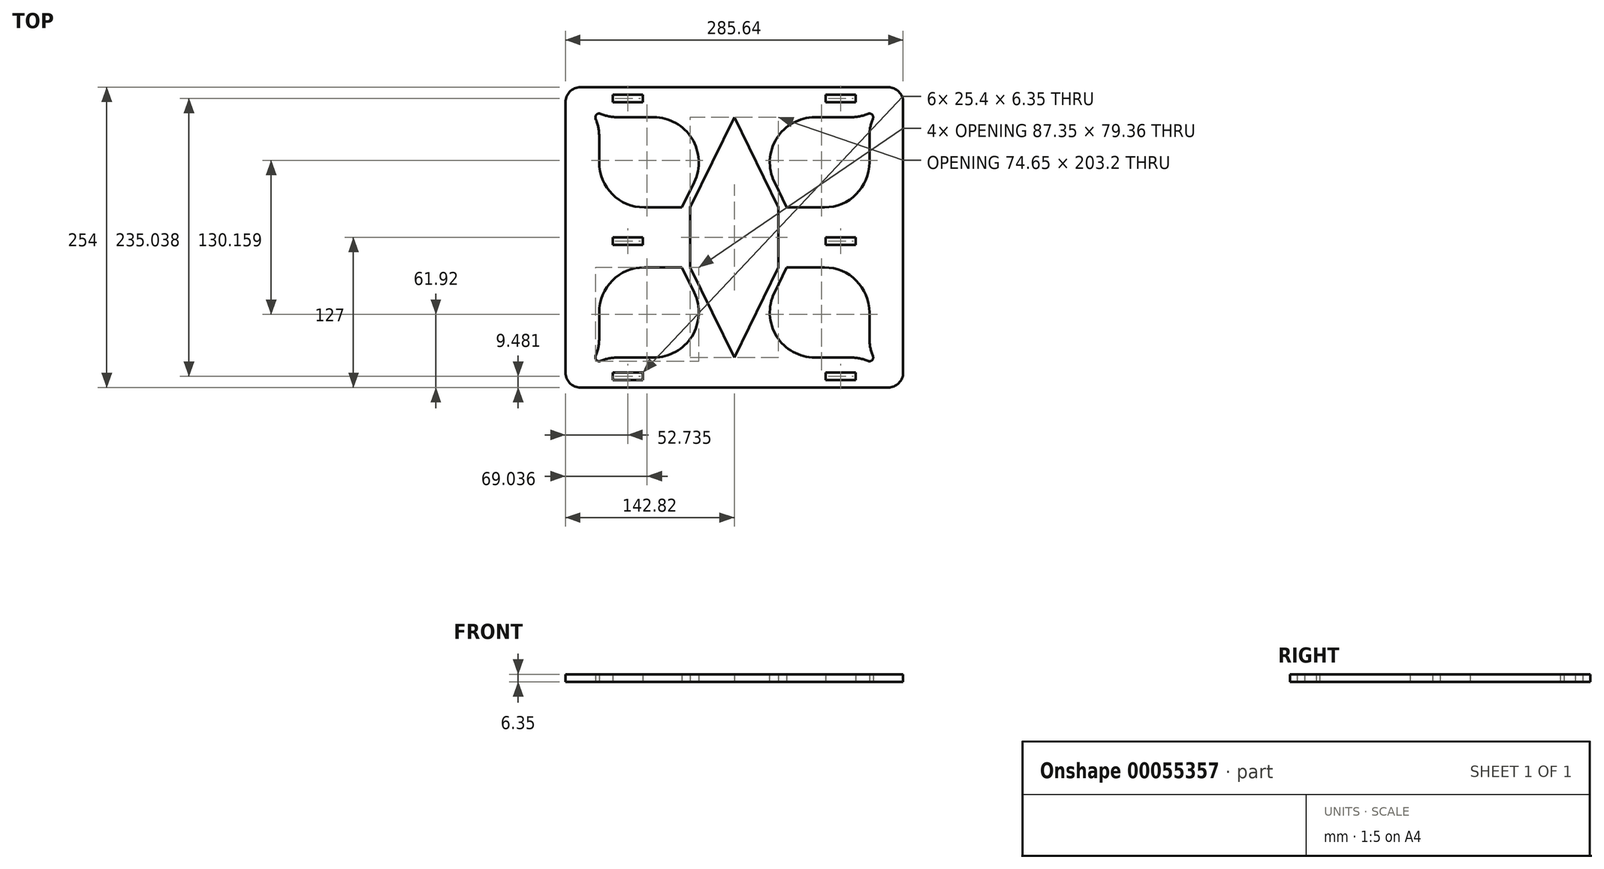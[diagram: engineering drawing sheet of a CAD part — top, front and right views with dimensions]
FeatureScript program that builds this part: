
annotation { "Feature Type Name" : "Feature", "Feature Type Description" : "" }
export const myFeature = defineFeature(function(context is Context, id is Id, definition is map)
    precondition{}
    {
        {
            var Q0;
            Q0=qCreatedBy(makeId("Top.planeOp"),FACE);
            var sketch = newSketch(context, id + "F0", { "sketchPlane" : qUnion([Q0])});
            skLineSegment(sketch, "E0.rect.bottom", {"start": v(130.12, 127) * mm, "end": v(-130.12, 127) * mm});
            skLineSegment(sketch, "E0.rect.top", {"start": v(130.12, -127) * mm, "end": v(-130.12, -127) * mm});
            skLineSegment(sketch, "E0.rect.left", {"start": v(142.82, 114.3) * mm, "end": v(142.82, -114.3) * mm});
            skLineSegment(sketch, "E0.rect.right", {"start": v(-142.82, 114.3) * mm, "end": v(-142.82, -114.3) * mm});
            skPoint(sketch, "E0.rect.middle", {"position": v(0, 0) * mm});
            skLineSegment(sketch, "E1", {"start": v(-142.82, 0) * mm, "end": v(-102.77, 0) * mm, "construction": true});
            skPoint(sketch, "E1.endSnap0", {"position": v(-142.82, 0) * mm});
            skPoint(sketch, "E2.visualSharp", {"position": v(-142.82, 127) * mm});
            skArc(sketch, "E2.filletArc", {"start": v(-130.12, 127) * mm, "mid": v(-139.1, 123.28) * mm, "end": v(-142.82, 114.3) * mm});
            skPoint(sketch, "E3.visualSharp", {"position": v(142.82, 127) * mm});
            skArc(sketch, "E3.filletArc", {"start": v(142.82, 114.3) * mm, "mid": v(139.1, 123.28) * mm, "end": v(130.12, 127) * mm});
            skPoint(sketch, "E4.visualSharp", {"position": v(142.82, -127) * mm});
            skArc(sketch, "E4.filletArc", {"start": v(130.12, -127) * mm, "mid": v(139.1, -123.28) * mm, "end": v(142.82, -114.3) * mm});
            skPoint(sketch, "E5.visualSharp", {"position": v(-142.82, -127) * mm});
            skArc(sketch, "E5.filletArc", {"start": v(-142.82, -114.3) * mm, "mid": v(-139.1, -123.28) * mm, "end": v(-130.12, -127) * mm});
            skLineSegment(sketch, "E6.rect.bottom", {"start": v(114.3, 101.6) * mm, "end": v(-114.3, 101.6) * mm});
            skLineSegment(sketch, "E6.rect.top", {"start": v(114.3, 25.4) * mm, "end": v(-114.3, 25.4) * mm});
            skLineSegment(sketch, "E6.rect.left", {"start": v(114.3, 101.6) * mm, "end": v(114.3, 25.4) * mm});
            skLineSegment(sketch, "E6.rect.right", {"start": v(-114.3, 101.6) * mm, "end": v(-114.3, 25.4) * mm});
            skPoint(sketch, "E6.rect.middle", {"position": v(0, 63.5) * mm});
            skLineSegment(sketch, "E7.MirrorCS", {"start": v(114.3, -101.6) * mm, "end": v(-114.3, -101.6) * mm});
            skLineSegment(sketch, "E8.MirrorCS", {"start": v(114.3, -101.6) * mm, "end": v(114.3, -25.4) * mm});
            skPoint(sketch, "E9.MirrorP", {"position": v(0, -63.5) * mm});
            skLineSegment(sketch, "E10.MirrorCS", {"start": v(-114.3, -101.6) * mm, "end": v(-114.3, -25.4) * mm});
            skLineSegment(sketch, "E11.MirrorCS", {"start": v(114.3, -25.4) * mm, "end": v(-114.3, -25.4) * mm});
            skLineSegment(sketch, "E12.MirrorCS", {"start": v(142.82, 0) * mm, "end": v(102.77, 0) * mm, "construction": true});
            skLineSegment(sketch, "E13.rect.bottom", {"start": v(37.33, 25.4) * mm, "end": v(-37.33, 25.4) * mm});
            skLineSegment(sketch, "E13.rect.top", {"start": v(37.33, -25.4) * mm, "end": v(-37.33, -25.4) * mm});
            skLineSegment(sketch, "E13.rect.left", {"start": v(37.33, 25.4) * mm, "end": v(37.33, -25.4) * mm});
            skLineSegment(sketch, "E13.rect.right", {"start": v(-37.33, 25.4) * mm, "end": v(-37.33, -25.4) * mm});
            skLineSegment(sketch, "E14", {"start": v(0, 101.6) * mm, "end": v(37.33, 25.4) * mm});
            skLineSegment(sketch, "E15.0", {"start": v(7.07, 101.6) * mm, "end": v(44.4, 25.4) * mm});
            skLineSegment(sketch, "E16.MirrorCS", {"start": v(0, 101.6) * mm, "end": v(-37.33, 25.4) * mm});
            skLineSegment(sketch, "E17.MirrorCS", {"start": v(-7.07, 101.6) * mm, "end": v(-44.4, 25.4) * mm});
            skLineSegment(sketch, "E18.MirrorCS", {"start": v(0, -101.6) * mm, "end": v(-37.33, -25.4) * mm});
            skLineSegment(sketch, "E19.MirrorCS", {"start": v(-7.07, -101.6) * mm, "end": v(-44.4, -25.4) * mm});
            skLineSegment(sketch, "E20.MirrorCS", {"start": v(7.07, -101.6) * mm, "end": v(44.4, -25.4) * mm});
            skLineSegment(sketch, "E21.MirrorCS", {"start": v(0, -101.6) * mm, "end": v(37.33, -25.4) * mm});
            skLineSegment(sketch, "E22", {"start": v(-142.82, 101.6) * mm, "end": v(-142.82, 127) * mm, "construction": true});
            skLineSegment(sketch, "E23", {"start": v(-142.82, 63.5) * mm, "end": v(142.82, 63.5) * mm, "construction": true});
            skPoint(sketch, "E23.endSnap0", {"position": v(114.3, 63.5) * mm});
            skCircle(sketch, "E24", {"center": v(-114.3, 101.6) * mm, "radius": 3.18 * mm});
            skCircle(sketch, "E25.MirrorC", {"center": v(114.3, 101.6) * mm, "radius": 3.18 * mm});
            skCircle(sketch, "E26.MirrorC", {"center": v(-114.3, -101.6) * mm, "radius": 3.18 * mm});
            skCircle(sketch, "E27.MirrorC", {"center": v(114.3, -101.6) * mm, "radius": 3.18 * mm});
            skLineSegment(sketch, "E28", {"start": v(-142.82, 63.5) * mm, "end": v(-142.82, 101.6) * mm, "construction": true});
            skLineSegment(sketch, "E29", {"start": v(-142.82, 82.55) * mm, "end": v(142.82, 82.55) * mm, "construction": true});
            skLineSegment(sketch, "E30", {"start": v(142.82, 82.55) * mm, "end": v(114.3, 82.55) * mm, "construction": true});
            skLineSegment(sketch, "E31", {"start": v(-142.82, 82.55) * mm, "end": v(-114.3, 82.55) * mm, "construction": true});
            skPoint(sketch, "E32.rect.middle", {"position": v(-102.77, 0) * mm});
            skLineSegment(sketch, "E33", {"start": v(0, 0) * mm, "end": v(0, 12.21) * mm, "construction": true});
            skPoint(sketch, "E34.MirrorP", {"position": v(102.77, 0) * mm});
            skLineSegment(sketch, "E35.MirrorCS", {"start": v(77.37, 0) * mm, "end": v(77.37, -6.35) * mm});
            skLineSegment(sketch, "E36", {"start": v(-102.77, -6.35) * mm, "end": v(-77.37, -6.35) * mm});
            skLineSegment(sketch, "E37", {"start": v(-102.77, 0) * mm, "end": v(-102.77, -6.35) * mm});
            skLineSegment(sketch, "E38", {"start": v(-77.37, 0) * mm, "end": v(-77.37, -6.35) * mm});
            skLineSegment(sketch, "E39", {"start": v(77.37, -6.35) * mm, "end": v(102.77, -6.35) * mm});
            skLineSegment(sketch, "E40", {"start": v(102.77, 0) * mm, "end": v(77.37, 0) * mm});
            skLineSegment(sketch, "E41", {"start": v(-102.77, 0) * mm, "end": v(-77.37, 0) * mm});
            skLineSegment(sketch, "E42", {"start": v(102.77, 0) * mm, "end": v(102.77, -6.35) * mm});
            skLineSegment(sketch, "E43", {"start": v(-142.84, -114.34) * mm, "end": v(-102.79, -114.34) * mm, "construction": true});
            skLineSegment(sketch, "E44", {"start": v(-102.79, -114.34) * mm, "end": v(-77.39, -114.34) * mm});
            skLineSegment(sketch, "E45", {"start": v(-77.39, -114.34) * mm, "end": v(-77.39, -120.7) * mm});
            skLineSegment(sketch, "E46", {"start": v(-102.79, -120.7) * mm, "end": v(-77.39, -120.7) * mm});
            skLineSegment(sketch, "E47", {"start": v(-102.79, -114.34) * mm, "end": v(-102.79, -120.7) * mm});
            skLineSegment(sketch, "E48.MirrorCS", {"start": v(102.79, -114.34) * mm, "end": v(77.39, -114.34) * mm});
            skLineSegment(sketch, "E49.MirrorCS", {"start": v(77.39, -114.34) * mm, "end": v(77.39, -120.7) * mm});
            skLineSegment(sketch, "E50.MirrorCS", {"start": v(102.79, -120.7) * mm, "end": v(77.39, -120.7) * mm});
            skLineSegment(sketch, "E51.MirrorCS", {"start": v(102.79, -114.34) * mm, "end": v(102.79, -120.7) * mm});
            skLineSegment(sketch, "E52.MirrorCS", {"start": v(77.39, 114.34) * mm, "end": v(77.39, 120.7) * mm});
            skLineSegment(sketch, "E53.MirrorCS", {"start": v(-102.79, 114.34) * mm, "end": v(-102.79, 120.7) * mm});
            skLineSegment(sketch, "E54.MirrorCS", {"start": v(102.79, 114.34) * mm, "end": v(102.79, 120.7) * mm});
            skLineSegment(sketch, "E55.MirrorCS", {"start": v(-77.39, 114.34) * mm, "end": v(-77.39, 120.7) * mm});
            skLineSegment(sketch, "E56.MirrorCS", {"start": v(102.79, 120.7) * mm, "end": v(77.39, 120.7) * mm});
            skLineSegment(sketch, "E57.MirrorCS", {"start": v(-102.79, 114.34) * mm, "end": v(-77.39, 114.34) * mm});
            skLineSegment(sketch, "E58.MirrorCS", {"start": v(-102.79, 120.7) * mm, "end": v(-77.39, 120.7) * mm});
            skLineSegment(sketch, "E59.MirrorCS", {"start": v(102.79, 114.34) * mm, "end": v(77.39, 114.34) * mm});
            skSolve(sketch);
        }
        {
            var Q0;
            {var subQ0=sQuery(id+"F0.wireOp",EDGE,"E16.MirrorCS");Q0=makeQuery(id+"F0.imprint","IMPRINT",FACE,{"disambiguationData":[TD([[makeQuery(id+"F0.imprint","IMPRINT",EDGE,{"derivedFrom":subQ0}),-1.0]])]});}
            var Q1;
            {var subQ0=sQuery(id+"F0.wireOp",EDGE,"E14");Q1=makeQuery(id+"F0.imprint","IMPRINT",FACE,{"disambiguationData":[TD([[makeQuery(id+"F0.imprint","IMPRINT",EDGE,{"derivedFrom":subQ0}),1.0]])]});}
            var Q2;
            {var subQ2=sQuery(id+"F0.wireOp",EDGE,"E20.MirrorCS");Q2=makeQuery(id+"F0.imprint","IMPRINT",FACE,{"disambiguationData":[TD([[makeQuery(id+"F0.imprint","IMPRINT",EDGE,{"derivedFrom":subQ2}),1.0]])]});}
            var Q3;
            {var subQ0=sQuery(id+"F0.wireOp",EDGE,"E18.MirrorCS");Q3=makeQuery(id+"F0.imprint","IMPRINT",FACE,{"disambiguationData":[TD([[makeQuery(id+"F0.imprint","IMPRINT",EDGE,{"derivedFrom":subQ0}),1.0]])]});}
            var Q4;
            Q4=makeQuery(id+"F0.imprint","IMPRINT",FACE,{"disambiguationData":[TD([[makeQuery(id+"F0.imprint","IMPRINT",EDGE,{"derivedFrom":sQuery(id+"F0.wireOp",EDGE,"384daab3-8df1-4059-9851-de201645e467")}),-1.0]])]});
            var Q5;
            Q5=makeQuery(id+"F0.imprint","IMPRINT",FACE,{"disambiguationData":[TD([[makeQuery(id+"F0.imprint","IMPRINT",EDGE,{"derivedFrom":sQuery(id+"F0.wireOp",EDGE,"E0.rect.bottom")}),1.0]])]});
            extrude(context, id + "F1", {"entities" : qUnion([Q0, Q1, Q2, Q3, Q4, Q5]), "depth" : 6.35 * mm});
        }
        {
            var Q0;
            Q0=makeQuery(id+"F1.opExtrude","SWEPT_EDGE",EDGE,{"disambiguationData":[OSD([sQuery(id+"F0.wireOp",EDGE,"E6.rect.bottom"),sQuery(id+"F0.wireOp",EDGE,"E6.rect.right")])]});
            var Q1;
            Q1=makeQuery(id+"F1.opExtrude","SWEPT_EDGE",EDGE,{"disambiguationData":[OSD([sQuery(id+"F0.wireOp",EDGE,"E6.rect.bottom"),sQuery(id+"F0.wireOp",EDGE,"E6.rect.left")])]});
            var Q2;
            Q2=makeQuery(id+"F1.opExtrude","SWEPT_EDGE",EDGE,{"disambiguationData":[OSD([sQuery(id+"F0.wireOp",EDGE,"E6.rect.top"),sQuery(id+"F0.wireOp",EDGE,"E6.rect.left")])]});
            var Q3;
            Q3=makeQuery(id+"F1.opExtrude","SWEPT_EDGE",EDGE,{"disambiguationData":[OSD([sQuery(id+"F0.wireOp",EDGE,"E6.rect.top"),sQuery(id+"F0.wireOp",EDGE,"E6.rect.right")])]});
            var Q4;
            Q4=makeQuery(id+"F1.opExtrude","SWEPT_EDGE",EDGE,{"disambiguationData":[OSD([sQuery(id+"F0.wireOp",EDGE,"E10.MirrorCS"),sQuery(id+"F0.wireOp",EDGE,"E11.MirrorCS")])]});
            var Q5;
            Q5=makeQuery(id+"F1.opExtrude","SWEPT_EDGE",EDGE,{"disambiguationData":[OSD([sQuery(id+"F0.wireOp",EDGE,"E8.MirrorCS"),sQuery(id+"F0.wireOp",EDGE,"E11.MirrorCS")])]});
            var Q6;
            Q6=makeQuery(id+"F1.opExtrude","SWEPT_EDGE",EDGE,{"disambiguationData":[OSD([sQuery(id+"F0.wireOp",EDGE,"E7.MirrorCS"),sQuery(id+"F0.wireOp",EDGE,"E8.MirrorCS")])]});
            var Q7;
            Q7=makeQuery(id+"F1.opExtrude","SWEPT_EDGE",EDGE,{"disambiguationData":[OSD([sQuery(id+"F0.wireOp",EDGE,"E7.MirrorCS"),sQuery(id+"F0.wireOp",EDGE,"E10.MirrorCS")])]});
            fillet(context, id + "F2", {"entities" : qUnion([Q0, Q1, Q2, Q3, Q4, Q5, Q6, Q7]), "radius" : 38.1 * mm, "tangentPropagation" : true, "allowEdgeOverflow" : false});
        }
    });
